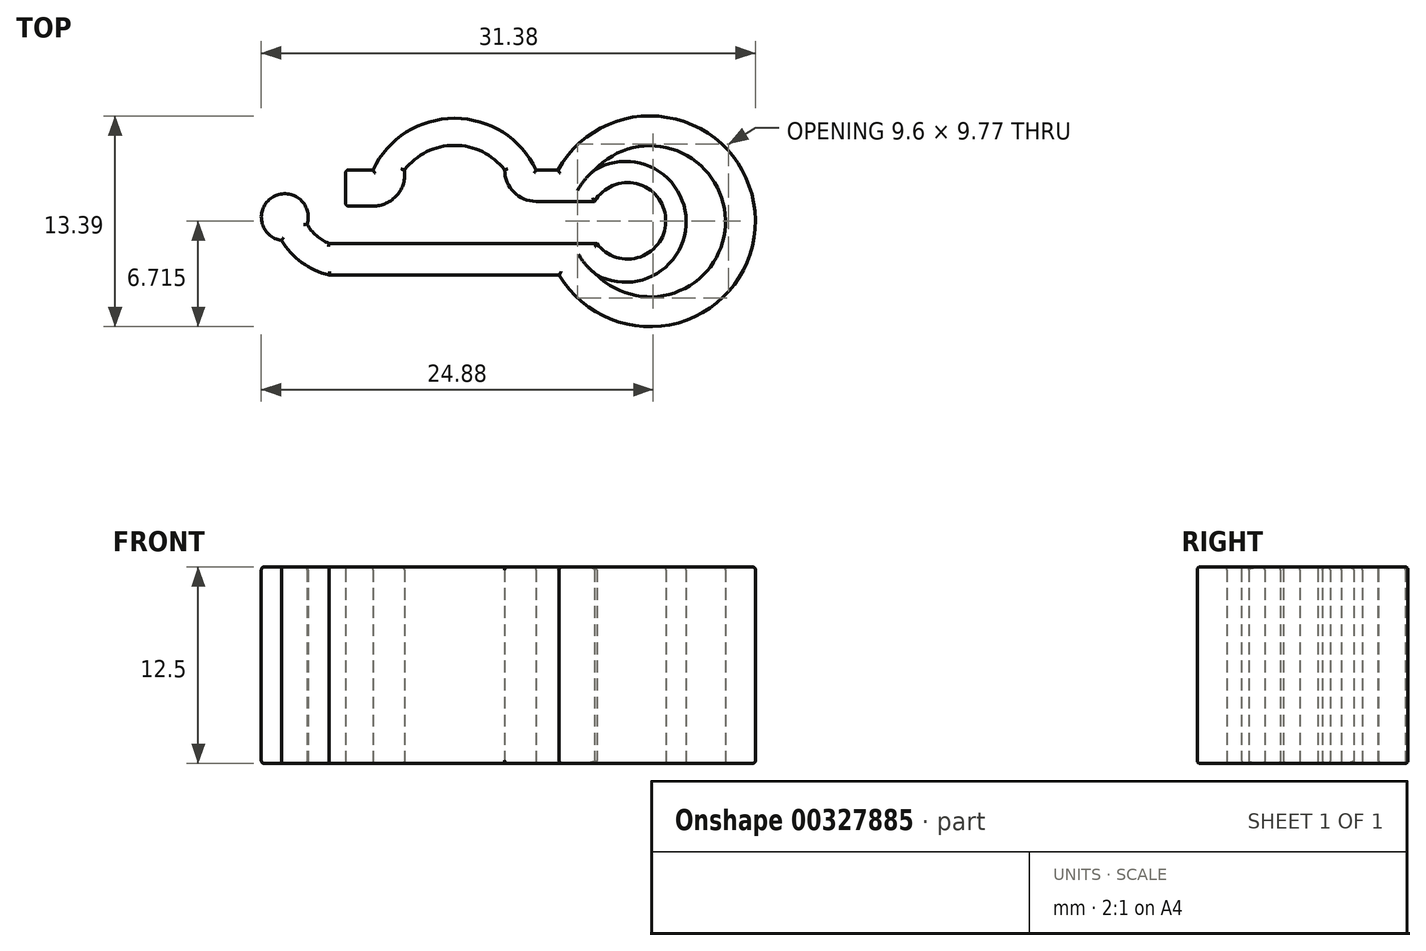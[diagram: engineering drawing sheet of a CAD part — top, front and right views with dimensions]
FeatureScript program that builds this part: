
annotation { "Feature Type Name" : "Feature", "Feature Type Description" : "" }
export const myFeature = defineFeature(function(context is Context, id is Id, definition is map)
    precondition{}
    {
        {
            var Q0;
            Q0=qCreatedBy(makeId("Top.planeOp"),FACE);
            var sketch = newSketch(context, id + "F0", { "sketchPlane" : qUnion([Q0])});
            skLineSegment(sketch, "E0.bottom", {"start": v(-8.76, -4.67) * mm, "end": v(8.24, -4.67) * mm});
            skLineSegment(sketch, "E0.top", {"start": v(-8.76, -6.67) * mm, "end": v(8.24, -6.67) * mm});
            skLineSegment(sketch, "E0.left", {"start": v(-8.76, -4.67) * mm, "end": v(-8.76, -6.67) * mm});
            skLineSegment(sketch, "E0.right", {"start": v(8.24, -4.67) * mm, "end": v(8.24, -6.67) * mm});
            skArc(sketch, "E1", {"start": v(-11.78, -4.48) * mm, "mid": v(-10.5, -5.88) * mm, "end": v(-8.76, -6.67) * mm});
            skArc(sketch, "E2", {"start": v(-10.16, -3.45) * mm, "mid": v(-9.57, -4.18) * mm, "end": v(-8.76, -4.67) * mm});
            skArc(sketch, "E3", {"start": v(-10.16, -3.45) * mm, "mid": v(-12.38, -1.75) * mm, "end": v(-11.78, -4.48) * mm});
            skLineSegment(sketch, "E4.bottom", {"start": v(8.1, 0) * mm, "end": v(4.39, 0) * mm});
            skLineSegment(sketch, "E4.top", {"start": v(8.1, -2) * mm, "end": v(4.39, -2) * mm});
            skLineSegment(sketch, "E4.left", {"start": v(8.1, 0) * mm, "end": v(8.1, -2) * mm});
            skLineSegment(sketch, "E4.right", {"start": v(4.39, 0) * mm, "end": v(4.39, -2) * mm});
            skArc(sketch, "E5", {"start": v(8.24, -6.67) * mm, "mid": v(13.91, -3.22) * mm, "end": v(8.1, 0) * mm});
            skArc(sketch, "E6", {"start": v(8.24, -4.67) * mm, "mid": v(12.62, -3.11) * mm, "end": v(8.1, -2) * mm});
            skArc(sketch, "E7", {"start": v(4.39, 0) * mm, "mid": v(-0.8, 3.28) * mm, "end": v(-5.98, 0) * mm});
            skArc(sketch, "E8", {"start": v(2.38, 0) * mm, "mid": v(2.97, -1.41) * mm, "end": v(4.39, -2) * mm});
            skArc(sketch, "E9", {"start": v(2.38, 0) * mm, "mid": v(-0.8, 1.56) * mm, "end": v(-3.98, 0) * mm});
            skLineSegment(sketch, "E10.bottom", {"start": v(-5.98, 0) * mm, "end": v(-7.72, 0) * mm});
            skLineSegment(sketch, "E10.top", {"start": v(-5.98, -2.3) * mm, "end": v(-7.72, -2.3) * mm});
            skLineSegment(sketch, "E10.left", {"start": v(-5.98, 0) * mm, "end": v(-5.98, -2.3) * mm});
            skLineSegment(sketch, "E10.right", {"start": v(-7.72, 0) * mm, "end": v(-7.72, -2.3) * mm});
            skArc(sketch, "E11", {"start": v(-5.98, -2.3) * mm, "mid": v(-4.46, -1.6) * mm, "end": v(-3.98, 0) * mm});
            skLineSegment(sketch, "E12", {"start": v(-0.8, 3.28) * mm, "end": v(24.74, 3.28) * mm, "construction": true});
            skLineSegment(sketch, "E13", {"start": v(8.1, -2) * mm, "end": v(25.13, -2) * mm, "construction": true});
            skArc(sketch, "E14", {"start": v(8.24, -6.67) * mm, "mid": v(16.41, -3.17) * mm, "end": v(8.1, 0) * mm});
            skArc(sketch, "E15", {"start": v(5.85, -6.67) * mm, "mid": v(18.31, -3.19) * mm, "end": v(5.77, 0) * mm});
            skSolve(sketch);
        }
        {
            var Q0;
            Q0 = qSketchRegion(id + "F0", true);
            extrude(context, id + "F1", {"entities" : qUnion([Q0]), "depth" : 12.5 * mm});
        }
        {
            var Q0;
            Q0=makeQuery(id+"F1.opExtrude","CAP_FACE",FACE,{"disambiguationData":[OSD([sQuery(id+"F0.wireOp",EDGE,"E0.bottom"),sQuery(id+"F0.wireOp",EDGE,"E0.top"),sQuery(id+"F0.wireOp",EDGE,"E1"),sQuery(id+"F0.wireOp",EDGE,"E2"),sQuery(id+"F0.wireOp",EDGE,"E3"),sQuery(id+"F0.wireOp",EDGE,"E4.bottom"),sQuery(id+"F0.wireOp",EDGE,"E4.top"),sQuery(id+"F0.wireOp",EDGE,"E5"),sQuery(id+"F0.wireOp",EDGE,"E6"),sQuery(id+"F0.wireOp",EDGE,"E7"),sQuery(id+"F0.wireOp",EDGE,"E8"),sQuery(id+"F0.wireOp",EDGE,"E9"),sQuery(id+"F0.wireOp",EDGE,"E10.bottom"),sQuery(id+"F0.wireOp",EDGE,"E10.top"),sQuery(id+"F0.wireOp",EDGE,"E10.right"),sQuery(id+"F0.wireOp",EDGE,"E11"),sQuery(id+"F0.wireOp",EDGE,"E14"),sQuery(id+"F0.wireOp",EDGE,"E15")])],"isStart":true});
            var Q1;
            Q1=makeQuery(id+"F1.opExtrude","SWEPT_FACE",FACE,{"disambiguationData":[OSD([sQuery(id+"F0.wireOp",EDGE,"E10.right")])]});
            var Q2;
            Q2=makeQuery(id+"F1.opExtrude","CAP_FACE",FACE,{"disambiguationData":[OSD([sQuery(id+"F0.wireOp",EDGE,"E0.bottom"),sQuery(id+"F0.wireOp",EDGE,"E0.top"),sQuery(id+"F0.wireOp",EDGE,"E1"),sQuery(id+"F0.wireOp",EDGE,"E2"),sQuery(id+"F0.wireOp",EDGE,"E3"),sQuery(id+"F0.wireOp",EDGE,"E4.bottom"),sQuery(id+"F0.wireOp",EDGE,"E4.top"),sQuery(id+"F0.wireOp",EDGE,"E5"),sQuery(id+"F0.wireOp",EDGE,"E6"),sQuery(id+"F0.wireOp",EDGE,"E7"),sQuery(id+"F0.wireOp",EDGE,"E8"),sQuery(id+"F0.wireOp",EDGE,"E9"),sQuery(id+"F0.wireOp",EDGE,"E10.bottom"),sQuery(id+"F0.wireOp",EDGE,"E10.top"),sQuery(id+"F0.wireOp",EDGE,"E10.right"),sQuery(id+"F0.wireOp",EDGE,"E11"),sQuery(id+"F0.wireOp",EDGE,"E14"),sQuery(id+"F0.wireOp",EDGE,"E15")])],"isStart":false});
            fillet(context, id + "F2", {"entities" : qUnion([Q0, Q1, Q2]), "radius" : 0.2 * mm, "tangentPropagation" : true, "allowEdgeOverflow" : false});
        }
    });
